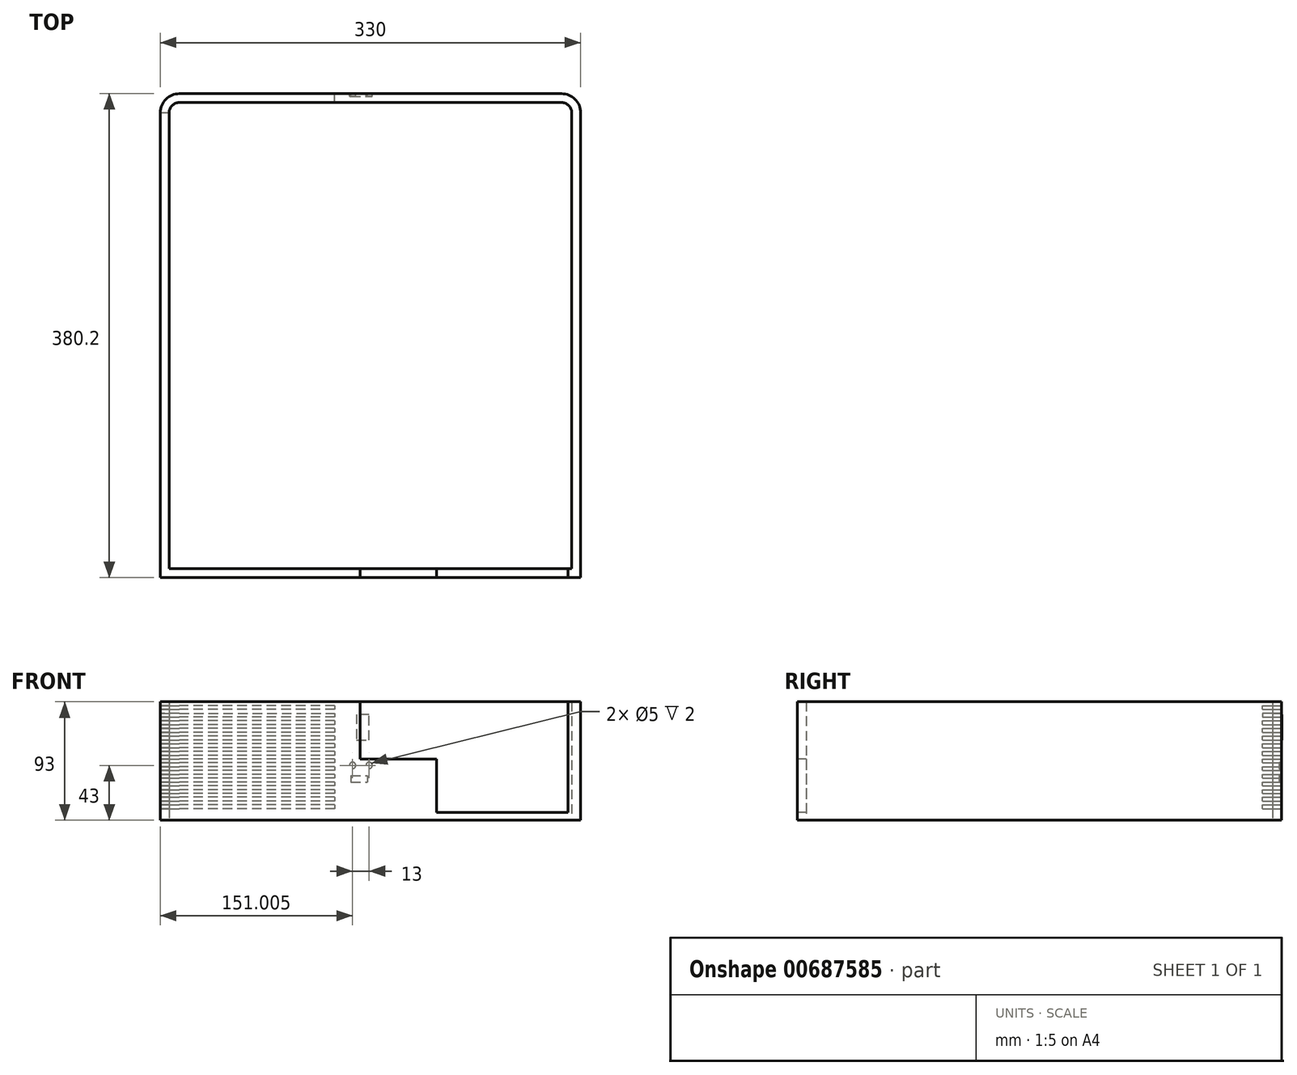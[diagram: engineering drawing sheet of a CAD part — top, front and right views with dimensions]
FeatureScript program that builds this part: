
annotation { "Feature Type Name" : "Feature", "Feature Type Description" : "" }
export const myFeature = defineFeature(function(context is Context, id is Id, definition is map)
    precondition{}
    {
        {
            var Q0;
            Q0=qCreatedBy(makeId("Top.planeOp"),FACE);
            var sketch = newSketch(context, id + "F0", { "sketchPlane" : qUnion([Q0])});
            skLineSegment(sketch, "E0.bottom", {"start": v(-232.36, 203.8) * mm, "end": v(67.64, 203.8) * mm});
            skLineSegment(sketch, "E0.top", {"start": v(-247.36, -176.2) * mm, "end": v(82.64, -176.2) * mm});
            skLineSegment(sketch, "E0.left", {"start": v(-247.36, 188.8) * mm, "end": v(-247.36, -176.2) * mm});
            skLineSegment(sketch, "E0.right", {"start": v(82.64, 188.8) * mm, "end": v(82.64, -176.2) * mm});
            skPoint(sketch, "E1.visualSharp", {"position": v(-247.36, 203.8) * mm});
            skArc(sketch, "E1.filletArc", {"start": v(-232.36, 203.8) * mm, "mid": v(-242.96, 199.41) * mm, "end": v(-247.36, 188.8) * mm});
            skPoint(sketch, "E2.visualSharp", {"position": v(82.64, 203.8) * mm});
            skArc(sketch, "E2.filletArc", {"start": v(82.64, 188.8) * mm, "mid": v(78.25, 199.41) * mm, "end": v(67.64, 203.8) * mm});
            skArc(sketch, "E3.0", {"start": v(-232.36, 196.8) * mm, "mid": v(-238.01, 194.46) * mm, "end": v(-240.36, 188.8) * mm});
            skArc(sketch, "E3.1", {"start": v(75.64, 188.8) * mm, "mid": v(73.3, 194.46) * mm, "end": v(67.64, 196.8) * mm});
            skLineSegment(sketch, "E3.2", {"start": v(75.64, 188.8) * mm, "end": v(75.64, -169.2) * mm});
            skLineSegment(sketch, "E3.3", {"start": v(-232.36, 196.8) * mm, "end": v(67.64, 196.8) * mm});
            skLineSegment(sketch, "E3.4", {"start": v(-240.36, -169.2) * mm, "end": v(75.64, -169.2) * mm});
            skLineSegment(sketch, "E3.5", {"start": v(-240.36, 188.8) * mm, "end": v(-240.36, -169.2) * mm});
            skSolve(sketch);
        }
        {
            var Q0;
            Q0 = qSketchRegion(id + "F0", true);
            extrude(context, id + "F1", {"entities" : qUnion([Q0]), "depth" : 93 * mm, "offsetDistance" : 25 * mm});
        }
        {
            var Q0;
            Q0=makeQuery(id+"F1.opExtrude","SWEPT_FACE",FACE,{"disambiguationData":[OSD([sQuery(id+"F0.wireOp",EDGE,"E0.top")])]});
            var sketch = newSketch(context, id + "F2", { "sketchPlane" : qUnion([Q0])});
            skLineSegment(sketch, "E4", {"start": v(72.64, 6) * mm, "end": v(-30.36, 6) * mm});
            skLineSegment(sketch, "E5.top", {"start": v(72.64, 100.52) * mm, "end": v(-30.36, 100.52) * mm});
            skLineSegment(sketch, "E5.left", {"start": v(72.64, 6) * mm, "end": v(72.64, 100.52) * mm});
            skLineSegment(sketch, "E5.right", {"start": v(-30.36, 6) * mm, "end": v(-30.36, 100.52) * mm});
            skPoint(sketch, "E6.orphan", {"position": v(82.64, 6) * mm});
            skLineSegment(sketch, "E7", {"start": v(-30.36, 6) * mm, "end": v(-30.36, 48) * mm});
            skLineSegment(sketch, "E8", {"start": v(-30.36, 48) * mm, "end": v(-90.36, 48) * mm});
            skLineSegment(sketch, "E9", {"start": v(-90.36, 48) * mm, "end": v(-90.36, 99.8) * mm});
            skLineSegment(sketch, "E10", {"start": v(-90.36, 99.8) * mm, "end": v(-30.36, 100.52) * mm});
            skSolve(sketch);
        }
        {
            var Q0;
            Q0 = qSketchRegion(id + "F2", true);
            extrude(context, id + "F3", {"entities" : qUnion([Q0]), "operationType" : NewBodyOperationType.REMOVE, "oppositeDirection" : true, "depth" : 25 * mm, "offsetDistance" : 25 * mm});
        }
        {
            var Q0;
            Q0=makeQuery(id+"F1.opExtrude","SWEPT_FACE",FACE,{"disambiguationData":[OSD([sQuery(id+"F0.wireOp",EDGE,"E0.bottom")])]});
            var sketch = newSketch(context, id + "F4", { "sketchPlane" : qUnion([Q0])});
            skLineSegment(sketch, "E11", {"start": v(110.36, 90) * mm, "end": v(247.36, 90) * mm});
            skLineSegment(sketch, "E12", {"start": v(110.36, 90) * mm, "end": v(110.36, 87) * mm});
            skLineSegment(sketch, "E13", {"start": v(110.36, 87) * mm, "end": v(247.36, 87) * mm});
            skLineSegment(sketch, "E14", {"start": v(247.36, 87) * mm, "end": v(247.36, 90) * mm});
            skLineSegment(sketch, "E15", {"start": v(247.36, 84) * mm, "end": v(247.36, 81) * mm});
            skLineSegment(sketch, "E16", {"start": v(247.36, 84) * mm, "end": v(110.36, 84) * mm});
            skLineSegment(sketch, "E17", {"start": v(110.36, 84) * mm, "end": v(110.36, 81) * mm});
            skLineSegment(sketch, "E18", {"start": v(110.36, 81) * mm, "end": v(247.36, 81) * mm});
            skLineSegment(sketch, "E19", {"start": v(110.36, 78) * mm, "end": v(247.36, 78) * mm});
            skLineSegment(sketch, "E20", {"start": v(110.36, 78) * mm, "end": v(110.36, 75) * mm});
            skLineSegment(sketch, "E21", {"start": v(110.36, 75) * mm, "end": v(247.36, 75) * mm});
            skLineSegment(sketch, "E22", {"start": v(247.36, 75) * mm, "end": v(247.36, 78) * mm});
            skLineSegment(sketch, "E23", {"start": v(110.36, 72) * mm, "end": v(247.36, 72) * mm});
            skLineSegment(sketch, "E24", {"start": v(110.36, 72) * mm, "end": v(110.36, 69) * mm});
            skLineSegment(sketch, "E25", {"start": v(110.36, 69) * mm, "end": v(247.36, 69) * mm});
            skLineSegment(sketch, "E26", {"start": v(247.36, 69) * mm, "end": v(247.36, 72) * mm});
            skLineSegment(sketch, "E27", {"start": v(110.36, 66) * mm, "end": v(247.36, 66) * mm});
            skLineSegment(sketch, "E28", {"start": v(110.36, 66) * mm, "end": v(110.36, 63) * mm});
            skLineSegment(sketch, "E29", {"start": v(110.36, 63) * mm, "end": v(247.36, 63) * mm});
            skLineSegment(sketch, "E30", {"start": v(247.36, 63) * mm, "end": v(247.36, 66) * mm});
            skLineSegment(sketch, "E31", {"start": v(110.36, 60) * mm, "end": v(247.36, 60) * mm});
            skLineSegment(sketch, "E32", {"start": v(110.36, 60) * mm, "end": v(110.36, 57) * mm});
            skLineSegment(sketch, "E33", {"start": v(110.36, 54) * mm, "end": v(247.36, 54) * mm});
            skLineSegment(sketch, "E34", {"start": v(247.36, 57) * mm, "end": v(247.36, 60) * mm});
            skLineSegment(sketch, "E35", {"start": v(110.36, 57) * mm, "end": v(247.36, 57) * mm});
            skLineSegment(sketch, "E36", {"start": v(110.36, 54) * mm, "end": v(110.36, 51) * mm});
            skLineSegment(sketch, "E37", {"start": v(110.36, 48) * mm, "end": v(247.36, 48) * mm});
            skLineSegment(sketch, "E38", {"start": v(247.36, 51) * mm, "end": v(247.36, 54) * mm});
            skLineSegment(sketch, "E39", {"start": v(110.36, 51) * mm, "end": v(247.36, 51) * mm});
            skLineSegment(sketch, "E40", {"start": v(110.36, 48) * mm, "end": v(110.36, 45) * mm});
            skLineSegment(sketch, "E41", {"start": v(110.36, 42) * mm, "end": v(247.36, 42) * mm});
            skLineSegment(sketch, "E42", {"start": v(247.36, 45) * mm, "end": v(247.36, 48) * mm});
            skLineSegment(sketch, "E43", {"start": v(110.36, 45) * mm, "end": v(247.36, 45) * mm});
            skLineSegment(sketch, "E44", {"start": v(110.36, 42) * mm, "end": v(110.36, 39) * mm});
            skLineSegment(sketch, "E45", {"start": v(110.36, 36) * mm, "end": v(247.36, 36) * mm});
            skLineSegment(sketch, "E46", {"start": v(110.36, 39) * mm, "end": v(247.36, 39) * mm});
            skLineSegment(sketch, "E47", {"start": v(247.36, 39) * mm, "end": v(247.36, 42) * mm});
            skLineSegment(sketch, "E48", {"start": v(110.36, 36) * mm, "end": v(110.36, 33) * mm});
            skLineSegment(sketch, "E49", {"start": v(110.36, 30) * mm, "end": v(247.36, 30) * mm});
            skLineSegment(sketch, "E50", {"start": v(247.36, 33) * mm, "end": v(247.36, 36) * mm});
            skLineSegment(sketch, "E51", {"start": v(110.36, 33) * mm, "end": v(247.36, 33) * mm});
            skLineSegment(sketch, "E52", {"start": v(110.36, 30) * mm, "end": v(110.36, 27) * mm});
            skLineSegment(sketch, "E53", {"start": v(110.36, 24) * mm, "end": v(247.36, 24) * mm});
            skLineSegment(sketch, "E54", {"start": v(247.36, 27) * mm, "end": v(247.36, 30) * mm});
            skLineSegment(sketch, "E55", {"start": v(110.36, 27) * mm, "end": v(247.36, 27) * mm});
            skLineSegment(sketch, "E56", {"start": v(110.36, 24) * mm, "end": v(110.36, 21) * mm});
            skLineSegment(sketch, "E57", {"start": v(110.36, 18) * mm, "end": v(247.36, 18) * mm});
            skLineSegment(sketch, "E58", {"start": v(247.36, 21) * mm, "end": v(247.36, 24) * mm});
            skLineSegment(sketch, "E59", {"start": v(110.36, 21) * mm, "end": v(247.36, 21) * mm});
            skLineSegment(sketch, "E60", {"start": v(110.36, 18) * mm, "end": v(110.36, 15) * mm});
            skLineSegment(sketch, "E61", {"start": v(110.36, 12) * mm, "end": v(247.36, 12) * mm});
            skLineSegment(sketch, "E62", {"start": v(247.36, 15) * mm, "end": v(247.36, 18) * mm});
            skLineSegment(sketch, "E63", {"start": v(110.36, 15) * mm, "end": v(247.36, 15) * mm});
            skLineSegment(sketch, "E64", {"start": v(110.36, 12) * mm, "end": v(110.36, 9) * mm});
            skLineSegment(sketch, "E65", {"start": v(110.36, 9) * mm, "end": v(247.36, 9) * mm});
            skLineSegment(sketch, "E66", {"start": v(247.36, 9) * mm, "end": v(247.36, 12) * mm});
            skPoint(sketch, "E67.start.orphan", {"position": v(247.36, 6) * mm});
            skSolve(sketch);
        }
        {
            var Q0;
            {var subQ0=sQuery(id+"F4.wireOp",EDGE,"E12");Q0=makeQuery(id+"F4.imprint","IMPRINT",FACE,{"disambiguationData":[TD([[makeQuery(id+"F4.imprint","IMPRINT",EDGE,{"derivedFrom":subQ0}),1.0]])]});}
            var Q1;
            {var subQ0=sQuery(id+"F4.wireOp",EDGE,"E14");Q1=makeQuery(id+"F4.imprint","IMPRINT",FACE,{"disambiguationData":[TD([[makeQuery(id+"F4.imprint","IMPRINT",EDGE,{"derivedFrom":subQ0}),1.0]])]});}
            extrude(context, id + "F5", {"entities" : qUnion([Q0, Q1]), "operationType" : NewBodyOperationType.REMOVE, "oppositeDirection" : true, "depth" : 15 * mm, "offsetDistance" : 25 * mm});
        }
        {
            var Q0;
            {var subQ0=sQuery(id+"F4.wireOp",EDGE,"E17");Q0=makeQuery(id+"F4.imprint","IMPRINT",FACE,{"disambiguationData":[TD([[makeQuery(id+"F4.imprint","IMPRINT",EDGE,{"derivedFrom":subQ0}),1.0]])]});}
            var Q1;
            {var subQ0=sQuery(id+"F4.wireOp",EDGE,"E15");Q1=makeQuery(id+"F4.imprint","IMPRINT",FACE,{"disambiguationData":[TD([[makeQuery(id+"F4.imprint","IMPRINT",EDGE,{"derivedFrom":subQ0}),-1.0]])]});}
            extrude(context, id + "F6", {"entities" : qUnion([Q0, Q1]), "operationType" : NewBodyOperationType.REMOVE, "oppositeDirection" : true, "depth" : 15 * mm, "offsetDistance" : 25 * mm});
        }
        {
            var Q0;
            {var subQ0=sQuery(id+"F4.wireOp",EDGE,"E20");Q0=makeQuery(id+"F4.imprint","IMPRINT",FACE,{"disambiguationData":[TD([[makeQuery(id+"F4.imprint","IMPRINT",EDGE,{"derivedFrom":subQ0}),1.0]])]});}
            var Q1;
            {var subQ0=sQuery(id+"F4.wireOp",EDGE,"E22");Q1=makeQuery(id+"F4.imprint","IMPRINT",FACE,{"disambiguationData":[TD([[makeQuery(id+"F4.imprint","IMPRINT",EDGE,{"derivedFrom":subQ0}),1.0]])]});}
            extrude(context, id + "F7", {"entities" : qUnion([Q0, Q1]), "operationType" : NewBodyOperationType.REMOVE, "oppositeDirection" : true, "depth" : 15 * mm, "offsetDistance" : 25 * mm});
        }
        {
            var Q0;
            {var subQ0=sQuery(id+"F4.wireOp",EDGE,"E24");Q0=makeQuery(id+"F4.imprint","IMPRINT",FACE,{"disambiguationData":[TD([[makeQuery(id+"F4.imprint","IMPRINT",EDGE,{"derivedFrom":subQ0}),1.0]])]});}
            var Q1;
            {var subQ0=sQuery(id+"F4.wireOp",EDGE,"E26");Q1=makeQuery(id+"F4.imprint","IMPRINT",FACE,{"disambiguationData":[TD([[makeQuery(id+"F4.imprint","IMPRINT",EDGE,{"derivedFrom":subQ0}),1.0]])]});}
            extrude(context, id + "F8", {"entities" : qUnion([Q0, Q1]), "operationType" : NewBodyOperationType.REMOVE, "oppositeDirection" : true, "depth" : 15 * mm, "offsetDistance" : 25 * mm});
        }
        {
            var Q0;
            {var subQ0=sQuery(id+"F4.wireOp",EDGE,"E28");Q0=makeQuery(id+"F4.imprint","IMPRINT",FACE,{"disambiguationData":[TD([[makeQuery(id+"F4.imprint","IMPRINT",EDGE,{"derivedFrom":subQ0}),1.0]])]});}
            var Q1;
            {var subQ0=sQuery(id+"F4.wireOp",EDGE,"E30");Q1=makeQuery(id+"F4.imprint","IMPRINT",FACE,{"disambiguationData":[TD([[makeQuery(id+"F4.imprint","IMPRINT",EDGE,{"derivedFrom":subQ0}),1.0]])]});}
            extrude(context, id + "F9", {"entities" : qUnion([Q0, Q1]), "operationType" : NewBodyOperationType.REMOVE, "oppositeDirection" : true, "depth" : 15 * mm, "offsetDistance" : 25 * mm});
        }
        {
            var Q0;
            {var subQ0=sQuery(id+"F4.wireOp",EDGE,"E32");Q0=makeQuery(id+"F4.imprint","IMPRINT",FACE,{"disambiguationData":[TD([[makeQuery(id+"F4.imprint","IMPRINT",EDGE,{"derivedFrom":subQ0}),1.0]])]});}
            var Q1;
            {var subQ0=sQuery(id+"F4.wireOp",EDGE,"E34");Q1=makeQuery(id+"F4.imprint","IMPRINT",FACE,{"disambiguationData":[TD([[makeQuery(id+"F4.imprint","IMPRINT",EDGE,{"derivedFrom":subQ0}),1.0]])]});}
            extrude(context, id + "F10", {"entities" : qUnion([Q0, Q1]), "operationType" : NewBodyOperationType.REMOVE, "oppositeDirection" : true, "depth" : 15 * mm, "offsetDistance" : 25 * mm});
        }
        {
            var Q0;
            {var subQ0=sQuery(id+"F4.wireOp",EDGE,"E36");Q0=makeQuery(id+"F4.imprint","IMPRINT",FACE,{"disambiguationData":[TD([[makeQuery(id+"F4.imprint","IMPRINT",EDGE,{"derivedFrom":subQ0}),1.0]])]});}
            var Q1;
            {var subQ0=sQuery(id+"F4.wireOp",EDGE,"E38");Q1=makeQuery(id+"F4.imprint","IMPRINT",FACE,{"disambiguationData":[TD([[makeQuery(id+"F4.imprint","IMPRINT",EDGE,{"derivedFrom":subQ0}),1.0]])]});}
            extrude(context, id + "F11", {"entities" : qUnion([Q0, Q1]), "operationType" : NewBodyOperationType.REMOVE, "oppositeDirection" : true, "depth" : 15 * mm, "offsetDistance" : 25 * mm});
        }
        {
            var Q0;
            {var subQ0=sQuery(id+"F4.wireOp",EDGE,"E40");Q0=makeQuery(id+"F4.imprint","IMPRINT",FACE,{"disambiguationData":[TD([[makeQuery(id+"F4.imprint","IMPRINT",EDGE,{"derivedFrom":subQ0}),1.0]])]});}
            var Q1;
            {var subQ0=sQuery(id+"F4.wireOp",EDGE,"E42");Q1=makeQuery(id+"F4.imprint","IMPRINT",FACE,{"disambiguationData":[TD([[makeQuery(id+"F4.imprint","IMPRINT",EDGE,{"derivedFrom":subQ0}),1.0]])]});}
            extrude(context, id + "F12", {"entities" : qUnion([Q0, Q1]), "operationType" : NewBodyOperationType.REMOVE, "oppositeDirection" : true, "depth" : 15 * mm, "offsetDistance" : 25 * mm});
        }
        {
            var Q0;
            {var subQ0=sQuery(id+"F4.wireOp",EDGE,"E44");Q0=makeQuery(id+"F4.imprint","IMPRINT",FACE,{"disambiguationData":[TD([[makeQuery(id+"F4.imprint","IMPRINT",EDGE,{"derivedFrom":subQ0}),1.0]])]});}
            var Q1;
            {var subQ0=sQuery(id+"F4.wireOp",EDGE,"E47");Q1=makeQuery(id+"F4.imprint","IMPRINT",FACE,{"disambiguationData":[TD([[makeQuery(id+"F4.imprint","IMPRINT",EDGE,{"derivedFrom":subQ0}),1.0]])]});}
            extrude(context, id + "F13", {"entities" : qUnion([Q0, Q1]), "operationType" : NewBodyOperationType.REMOVE, "oppositeDirection" : true, "depth" : 15 * mm, "offsetDistance" : 25 * mm});
        }
        {
            var Q0;
            {var subQ0=sQuery(id+"F4.wireOp",EDGE,"E48");Q0=makeQuery(id+"F4.imprint","IMPRINT",FACE,{"disambiguationData":[TD([[makeQuery(id+"F4.imprint","IMPRINT",EDGE,{"derivedFrom":subQ0}),1.0]])]});}
            var Q1;
            {var subQ0=sQuery(id+"F4.wireOp",EDGE,"E50");Q1=makeQuery(id+"F4.imprint","IMPRINT",FACE,{"disambiguationData":[TD([[makeQuery(id+"F4.imprint","IMPRINT",EDGE,{"derivedFrom":subQ0}),1.0]])]});}
            extrude(context, id + "F14", {"entities" : qUnion([Q0, Q1]), "operationType" : NewBodyOperationType.REMOVE, "oppositeDirection" : true, "depth" : 15 * mm, "offsetDistance" : 25 * mm});
        }
        {
            var Q0;
            {var subQ0=sQuery(id+"F4.wireOp",EDGE,"E52");Q0=makeQuery(id+"F4.imprint","IMPRINT",FACE,{"disambiguationData":[TD([[makeQuery(id+"F4.imprint","IMPRINT",EDGE,{"derivedFrom":subQ0}),1.0]])]});}
            var Q1;
            {var subQ0=sQuery(id+"F4.wireOp",EDGE,"E54");Q1=makeQuery(id+"F4.imprint","IMPRINT",FACE,{"disambiguationData":[TD([[makeQuery(id+"F4.imprint","IMPRINT",EDGE,{"derivedFrom":subQ0}),1.0]])]});}
            extrude(context, id + "F15", {"entities" : qUnion([Q0, Q1]), "operationType" : NewBodyOperationType.REMOVE, "oppositeDirection" : true, "depth" : 15 * mm, "offsetDistance" : 25 * mm});
        }
        {
            var Q0;
            {var subQ0=sQuery(id+"F4.wireOp",EDGE,"E56");Q0=makeQuery(id+"F4.imprint","IMPRINT",FACE,{"disambiguationData":[TD([[makeQuery(id+"F4.imprint","IMPRINT",EDGE,{"derivedFrom":subQ0}),1.0]])]});}
            var Q1;
            {var subQ0=sQuery(id+"F4.wireOp",EDGE,"E58");Q1=makeQuery(id+"F4.imprint","IMPRINT",FACE,{"disambiguationData":[TD([[makeQuery(id+"F4.imprint","IMPRINT",EDGE,{"derivedFrom":subQ0}),1.0]])]});}
            extrude(context, id + "F16", {"entities" : qUnion([Q0, Q1]), "operationType" : NewBodyOperationType.REMOVE, "oppositeDirection" : true, "depth" : 15 * mm, "offsetDistance" : 25 * mm});
        }
        {
            var Q0;
            {var subQ0=sQuery(id+"F4.wireOp",EDGE,"E60");Q0=makeQuery(id+"F4.imprint","IMPRINT",FACE,{"disambiguationData":[TD([[makeQuery(id+"F4.imprint","IMPRINT",EDGE,{"derivedFrom":subQ0}),1.0]])]});}
            var Q1;
            {var subQ0=sQuery(id+"F4.wireOp",EDGE,"E62");Q1=makeQuery(id+"F4.imprint","IMPRINT",FACE,{"disambiguationData":[TD([[makeQuery(id+"F4.imprint","IMPRINT",EDGE,{"derivedFrom":subQ0}),1.0]])]});}
            extrude(context, id + "F17", {"entities" : qUnion([Q0, Q1]), "operationType" : NewBodyOperationType.REMOVE, "oppositeDirection" : true, "depth" : 15 * mm, "offsetDistance" : 25 * mm});
        }
        {
            var Q0;
            {var subQ0=sQuery(id+"F4.wireOp",EDGE,"E64");Q0=makeQuery(id+"F4.imprint","IMPRINT",FACE,{"disambiguationData":[TD([[makeQuery(id+"F4.imprint","IMPRINT",EDGE,{"derivedFrom":subQ0}),1.0]])]});}
            var Q1;
            {var subQ0=sQuery(id+"F4.wireOp",EDGE,"E66");Q1=makeQuery(id+"F4.imprint","IMPRINT",FACE,{"disambiguationData":[TD([[makeQuery(id+"F4.imprint","IMPRINT",EDGE,{"derivedFrom":subQ0}),1.0]])]});}
            extrude(context, id + "F18", {"entities" : qUnion([Q0, Q1]), "operationType" : NewBodyOperationType.REMOVE, "oppositeDirection" : true, "depth" : 15 * mm, "offsetDistance" : 25 * mm});
        }
        {
            var Q0;
            Q0=makeQuery(id+"F1.opExtrude","SWEPT_FACE",FACE,{"disambiguationData":[OSD([sQuery(id+"F0.wireOp",EDGE,"E0.bottom")])]});
            var sketch = newSketch(context, id + "F19", { "sketchPlane" : qUnion([Q0])});
            skLineSegment(sketch, "E68", {"start": v(93.36, 83) * mm, "end": v(93.36, 63) * mm});
            skLineSegment(sketch, "E69", {"start": v(93.36, 63) * mm, "end": v(83.36, 63) * mm});
            skLineSegment(sketch, "E70", {"start": v(83.36, 63) * mm, "end": v(83.36, 83) * mm});
            skLineSegment(sketch, "E71", {"start": v(83.36, 83) * mm, "end": v(93.36, 83) * mm});
            skSolve(sketch);
        }
        {
            var Q0;
            Q0 = qSketchRegion(id + "F19", true);
            extrude(context, id + "F20", {"entities" : qUnion([Q0]), "operationType" : NewBodyOperationType.ADD, "depth" : 0.2 * mm, "offsetDistance" : 25 * mm});
        }
        {
            var Q0;
            Q0=makeQuery(id+"F1.opExtrude","SWEPT_FACE",FACE,{"disambiguationData":[OSD([sQuery(id+"F0.wireOp",EDGE,"E0.bottom")])]});
            var sketch = newSketch(context, id + "F21", { "sketchPlane" : qUnion([Q0])});
            skCircle(sketch, "E72", {"center": v(96.36, 43) * mm, "radius": 2.5 * mm});
            skCircle(sketch, "E73", {"center": v(83.36, 43) * mm, "radius": 2.5 * mm});
            skSolve(sketch);
        }
        {
            var Q0;
            Q0=makeQuery(id+"F21.imprint","IMPRINT",FACE,{"disambiguationData":[TD([[makeQuery(id+"F21.imprint","IMPRINT",EDGE,{"derivedFrom":sQuery(id+"F21.wireOp",EDGE,"E73")}),1.0]])]});
            extrude(context, id + "F22", {"entities" : qUnion([Q0]), "operationType" : NewBodyOperationType.REMOVE, "oppositeDirection" : true, "depth" : 2 * mm, "offsetDistance" : 25 * mm});
        }
        {
            var Q0;
            Q0=makeQuery(id+"F21.imprint","IMPRINT",FACE,{"disambiguationData":[TD([[makeQuery(id+"F21.imprint","IMPRINT",EDGE,{"derivedFrom":sQuery(id+"F21.wireOp",EDGE,"E72")}),1.0]])]});
            extrude(context, id + "F23", {"entities" : qUnion([Q0]), "operationType" : NewBodyOperationType.REMOVE, "oppositeDirection" : true, "depth" : 2 * mm, "offsetDistance" : 25 * mm});
        }
        {
            var Q0;
            Q0=makeQuery(id+"F1.opExtrude","SWEPT_FACE",FACE,{"disambiguationData":[OSD([sQuery(id+"F0.wireOp",EDGE,"E0.bottom")])]});
            var sketch = newSketch(context, id + "F24", { "sketchPlane" : qUnion([Q0])});
            skLineSegment(sketch, "E74.bottom", {"start": v(97.72, 34.87) * mm, "end": v(84.72, 34.87) * mm});
            skLineSegment(sketch, "E74.top", {"start": v(97.72, 29.87) * mm, "end": v(84.72, 29.87) * mm});
            skLineSegment(sketch, "E74.left", {"start": v(97.72, 34.87) * mm, "end": v(97.72, 29.87) * mm});
            skLineSegment(sketch, "E74.right", {"start": v(84.72, 34.87) * mm, "end": v(84.72, 29.87) * mm});
            skSolve(sketch);
        }
        {
            var Q0;
            Q0 = qSketchRegion(id + "F24", true);
            extrude(context, id + "F25", {"entities" : qUnion([Q0]), "operationType" : NewBodyOperationType.REMOVE, "oppositeDirection" : true, "depth" : 2 * mm, "offsetDistance" : 25 * mm});
        }
    });
